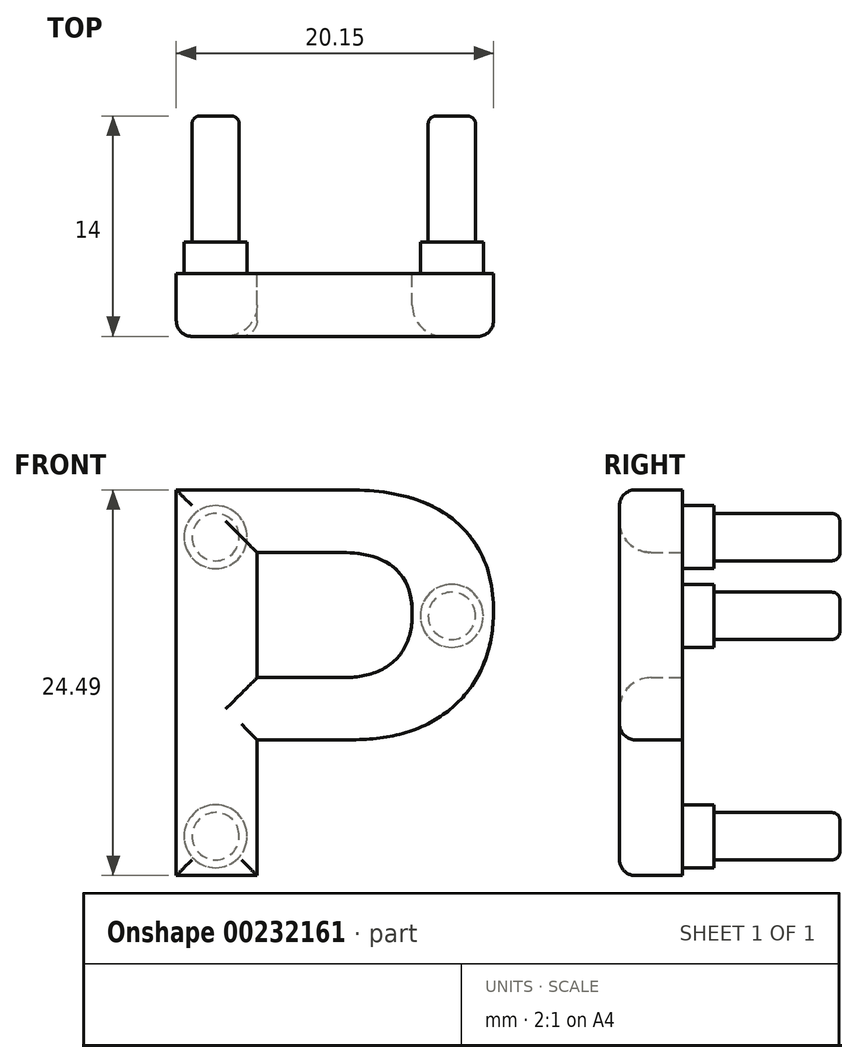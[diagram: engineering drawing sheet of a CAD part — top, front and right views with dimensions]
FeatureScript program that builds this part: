
annotation { "Feature Type Name" : "Feature", "Feature Type Description" : "" }
export const myFeature = defineFeature(function(context is Context, id is Id, definition is map)
    precondition{}
    {
        {
            var Q0;
            Q0=qCreatedBy(makeId("Front.planeOp"),FACE);
            var sketch = newSketch(context, id + "F0", { "sketchPlane" : qUnion([Q0])});
            skText(sketch, "E0", { "text": "P", "fontName": "Arimo-Bold.ttf"});
            const initialGuessF0  = {"E0": [-0.00703, -0.0169, 1, 0, 0.02563]};
            skSetInitialGuess(sketch, initialGuessF0);
            skSolve(sketch);
        }
        {
            var Q0;
            Q0=makeQuery(id+"F0.imprint","IMPRINT",FACE,{"disambiguationData":[TD([[makeQuery(id+"F0.imprint","IMPRINT",EDGE,{"derivedFrom":sQuery(id+"F0.wireOp",EDGE,"E0.sketch_text.stroke-0")}),-1.0]])]});
            extrude(context, id + "F1", {"entities" : qUnion([Q0]), "depth" : 4 * mm});
        }
        {
            var Q0;
            Q0=makeQuery(id+"F1.opExtrude","CAP_EDGE",EDGE,{"disambiguationData":[OSD([sQuery(id+"F0.wireOp",EDGE,"E0.sketch_text.stroke-13")])],"isStart":false});
            var Q1;
            Q1=makeQuery(id+"F1.opExtrude","CAP_EDGE",EDGE,{"disambiguationData":[OSD([sQuery(id+"F0.wireOp",EDGE,"E0.sketch_text.stroke-12")])],"isStart":false});
            fillet(context, id + "F2", {"entities" : qUnion([Q0, Q1]), "radius" : 2 * mm, "tangentPropagation" : true, "allowEdgeOverflow" : false});
        }
        {
            var Q0;
            Q0=makeQuery(id+"F1.opExtrude","CAP_EDGE",EDGE,{"disambiguationData":[OSD([sQuery(id+"F0.wireOp",EDGE,"E0.sketch_text.stroke-4")])],"isStart":false});
            var Q1;
            Q1=makeQuery(id+"F1.opExtrude","CAP_EDGE",EDGE,{"disambiguationData":[OSD([sQuery(id+"F0.wireOp",EDGE,"E0.sketch_text.stroke-5")])],"isStart":false});
            var Q2;
            Q2=makeQuery(id+"F1.opExtrude","CAP_EDGE",EDGE,{"disambiguationData":[OSD([sQuery(id+"F0.wireOp",EDGE,"E0.sketch_text.stroke-6")])],"isStart":false});
            var Q3;
            Q3=makeQuery(id+"F1.opExtrude","CAP_EDGE",EDGE,{"disambiguationData":[OSD([sQuery(id+"F0.wireOp",EDGE,"E0.sketch_text.stroke-9")])],"isStart":false});
            fillet(context, id + "F3", {"entities" : qUnion([Q0, Q1, Q2, Q3]), "radius" : 1 * mm, "tangentPropagation" : true, "allowEdgeOverflow" : false});
        }
        {
            var Q0;
            Q0=makeQuery(id+"F1.opExtrude","CAP_FACE",FACE,{"disambiguationData":[OSD([sQuery(id+"F0.wireOp",EDGE,"E0.sketch_text.stroke-0"),sQuery(id+"F0.wireOp",EDGE,"E0.sketch_text.stroke-1"),sQuery(id+"F0.wireOp",EDGE,"E0.sketch_text.stroke-2"),sQuery(id+"F0.wireOp",EDGE,"E0.sketch_text.stroke-3"),sQuery(id+"F0.wireOp",EDGE,"E0.sketch_text.stroke-4"),sQuery(id+"F0.wireOp",EDGE,"E0.sketch_text.stroke-5"),sQuery(id+"F0.wireOp",EDGE,"E0.sketch_text.stroke-6"),sQuery(id+"F0.wireOp",EDGE,"E0.sketch_text.stroke-7"),sQuery(id+"F0.wireOp",EDGE,"E0.sketch_text.stroke-8"),sQuery(id+"F0.wireOp",EDGE,"E0.sketch_text.stroke-9"),sQuery(id+"F0.wireOp",EDGE,"E0.sketch_text.stroke-10"),sQuery(id+"F0.wireOp",EDGE,"E0.sketch_text.stroke-11"),sQuery(id+"F0.wireOp",EDGE,"E0.sketch_text.stroke-12"),sQuery(id+"F0.wireOp",EDGE,"E0.sketch_text.stroke-13"),sQuery(id+"F0.wireOp",EDGE,"E0.sketch_text.stroke-14"),sQuery(id+"F0.wireOp",EDGE,"E0.sketch_text.stroke-15")])],"isStart":true});
            var sketch = newSketch(context, id + "F4", { "sketchPlane" : qUnion([Q0])});
            skCircle(sketch, "E1", {"center": v(2.15, 4.6) * mm, "radius": 1.5 * mm});
            skCircle(sketch, "E2", {"center": v(-12.85, -0.4) * mm, "radius": 1.5 * mm});
            skCircle(sketch, "E3", {"center": v(2.15, -14.4) * mm, "radius": 1.5 * mm});
            skLineSegment(sketch, "E4", {"start": v(4.65, 7.6) * mm, "end": v(-24.3, 7.6) * mm});
            skLineSegment(sketch, "E5", {"start": v(4.65, 7.6) * mm, "end": v(4.65, -4.31) * mm});
            skSolve(sketch);
        }
        {
            var Q0;
            Q0 = qSketchRegion(id + "F4", true);
            extrude(context, id + "F5", {"entities" : qUnion([Q0]), "operationType" : NewBodyOperationType.ADD, "depth" : 10 * mm});
        }
        {
            var Q0;
            Q0=makeQuery(id+"F1.opExtrude","CAP_FACE",FACE,{"disambiguationData":[OSD([sQuery(id+"F0.wireOp",EDGE,"E0.sketch_text.stroke-0"),sQuery(id+"F0.wireOp",EDGE,"E0.sketch_text.stroke-1"),sQuery(id+"F0.wireOp",EDGE,"E0.sketch_text.stroke-2"),sQuery(id+"F0.wireOp",EDGE,"E0.sketch_text.stroke-3"),sQuery(id+"F0.wireOp",EDGE,"E0.sketch_text.stroke-4"),sQuery(id+"F0.wireOp",EDGE,"E0.sketch_text.stroke-5"),sQuery(id+"F0.wireOp",EDGE,"E0.sketch_text.stroke-6"),sQuery(id+"F0.wireOp",EDGE,"E0.sketch_text.stroke-7"),sQuery(id+"F0.wireOp",EDGE,"E0.sketch_text.stroke-8"),sQuery(id+"F0.wireOp",EDGE,"E0.sketch_text.stroke-9"),sQuery(id+"F0.wireOp",EDGE,"E0.sketch_text.stroke-10"),sQuery(id+"F0.wireOp",EDGE,"E0.sketch_text.stroke-11"),sQuery(id+"F0.wireOp",EDGE,"E0.sketch_text.stroke-12"),sQuery(id+"F0.wireOp",EDGE,"E0.sketch_text.stroke-13"),sQuery(id+"F0.wireOp",EDGE,"E0.sketch_text.stroke-14"),sQuery(id+"F0.wireOp",EDGE,"E0.sketch_text.stroke-15")])],"isStart":true});
            var sketch = newSketch(context, id + "F6", { "sketchPlane" : qUnion([Q0])});
            skCircle(sketch, "E6", {"center": v(2.15, 4.6) * mm, "radius": 2 * mm});
            skCircle(sketch, "E7", {"center": v(-12.85, -0.4) * mm, "radius": 2 * mm});
            skCircle(sketch, "E8", {"center": v(2.15, -14.4) * mm, "radius": 2 * mm});
            skSolve(sketch);
        }
        {
            var Q0;
            Q0 = qSketchRegion(id + "F6", true);
            extrude(context, id + "F7", {"entities" : qUnion([Q0]), "operationType" : NewBodyOperationType.ADD, "depth" : 2 * mm});
        }
        {
            var Q0;
            Q0=makeQuery(id+"F5.opExtrude","CAP_EDGE",EDGE,{"disambiguationData":[OSD([sQuery(id+"F4.wireOp",EDGE,"jWUpQEvW-GLhT-3lxm-mQaN-SJj0nUYI6NvJ")])],"isStart":false});
            var Q1;
            Q1=makeQuery(id+"F5.opExtrude","CAP_EDGE",EDGE,{"disambiguationData":[OSD([sQuery(id+"F4.wireOp",EDGE,"E1")])],"isStart":false});
            var Q2;
            Q2=makeQuery(id+"F5.opExtrude","CAP_EDGE",EDGE,{"disambiguationData":[OSD([sQuery(id+"F4.wireOp",EDGE,"E3")])],"isStart":false});
            var Q3;
            Q3=makeQuery(id+"F5.opExtrude","CAP_EDGE",EDGE,{"disambiguationData":[OSD([sQuery(id+"F4.wireOp",EDGE,"E2")])],"isStart":false});
            var Q4;
            Q4=makeQuery(id+"F5.opExtrude","CAP_EDGE",EDGE,{"disambiguationData":[OSD([sQuery(id+"F4.wireOp",EDGE,"uctb2KFl-K2Ep-BzR8-qdpg-GnC9occJ5a8t")])],"isStart":false});
            fillet(context, id + "F8", {"entities" : qUnion([Q0, Q1, Q2, Q3, Q4]), "radius" : 0.5 * mm, "tangentPropagation" : true, "allowEdgeOverflow" : false});
        }
    });
